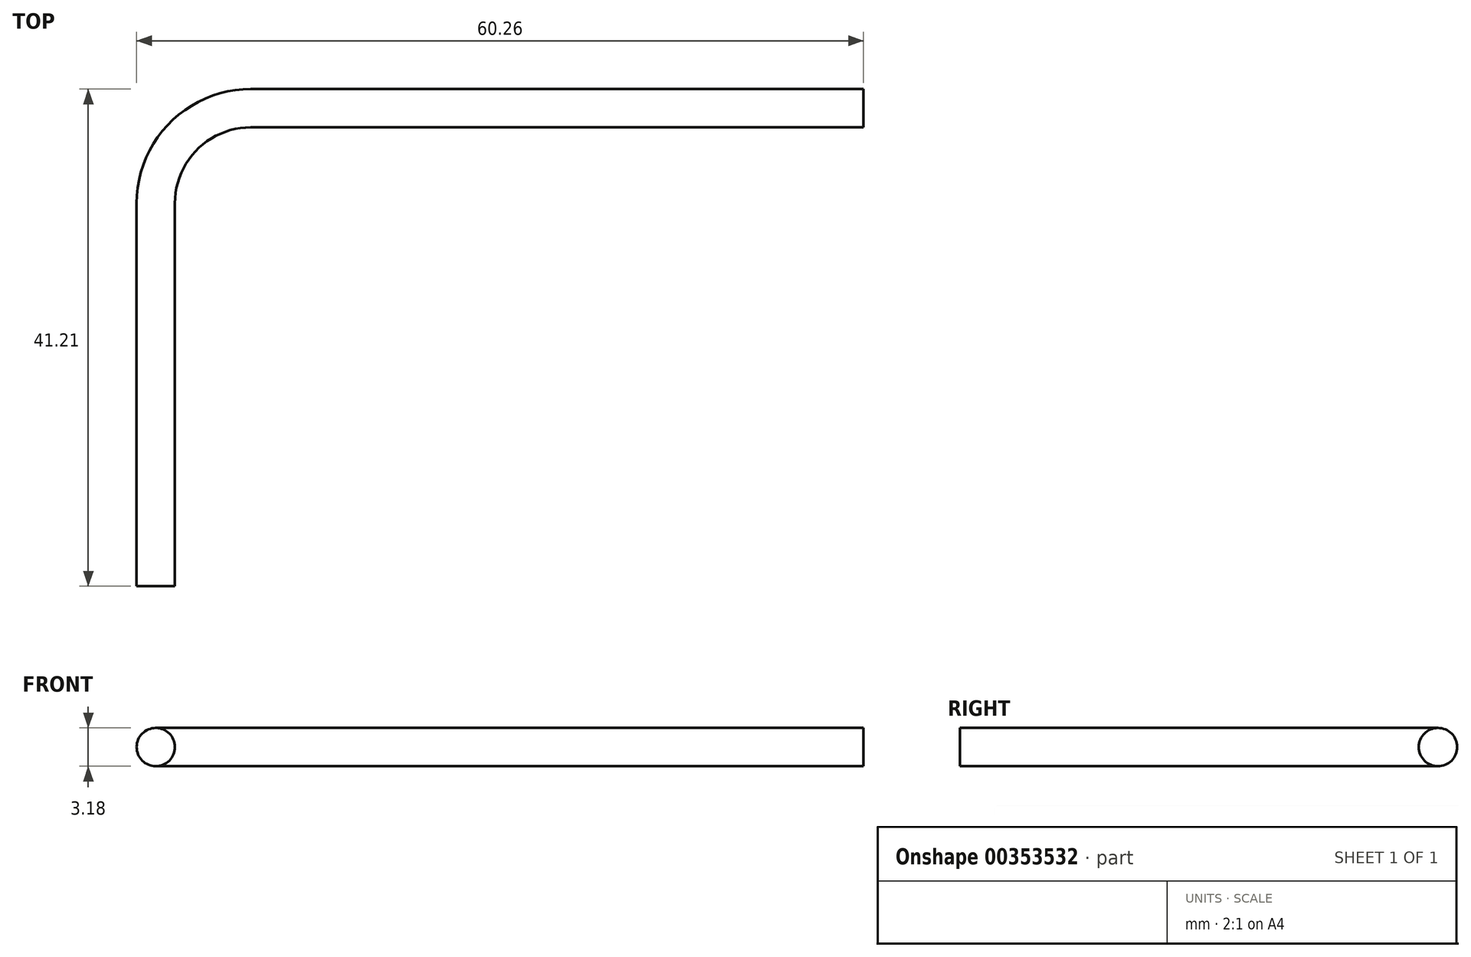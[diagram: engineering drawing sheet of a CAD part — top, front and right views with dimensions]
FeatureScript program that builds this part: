
annotation { "Feature Type Name" : "Feature", "Feature Type Description" : "" }
export const myFeature = defineFeature(function(context is Context, id is Id, definition is map)
    precondition{}
    {
        {
            var Q0;
            Q0=qCreatedBy(makeId("Top.planeOp"),FACE);
            var sketch = newSketch(context, id + "F0", { "sketchPlane" : qUnion([Q0])});
            skLineSegment(sketch, "E0", {"start": v(0, 0) * mm, "end": v(0, 31.75) * mm});
            skLineSegment(sketch, "E1", {"start": v(7.87, 0) * mm, "end": v(7.87, 56.73) * mm, "construction": true});
            skArc(sketch, "E2", {"start": v(0, 31.75) * mm, "mid": v(2.3, 37.32) * mm, "end": v(7.87, 39.62) * mm});
            skLineSegment(sketch, "E3", {"start": v(7.87, 39.62) * mm, "end": v(58.67, 39.62) * mm});
            skSolve(sketch);
        }
        {
            var Q0;
            Q0=qCreatedBy(makeId("Front.planeOp"),FACE);
            var sketch = newSketch(context, id + "F1", { "sketchPlane" : qUnion([Q0])});
            skCircle(sketch, "E4", {"center": v(0, 0) * mm, "radius": 1.59 * mm});
            skSolve(sketch);
        }
        {
            var Q0;
            Q0 = qSketchRegion(id + "F1", true);
            var Q1;
            Q1 = qConstructionFilter(qBodyType(qCreatedBy(id + "F0" ,EDGE), BodyType.WIRE), ConstructionObject.NO);
            sweep(context, id + "F2", {"profiles" : qUnion([Q0]), "path" : qUnion([Q1])});
        }
    });
